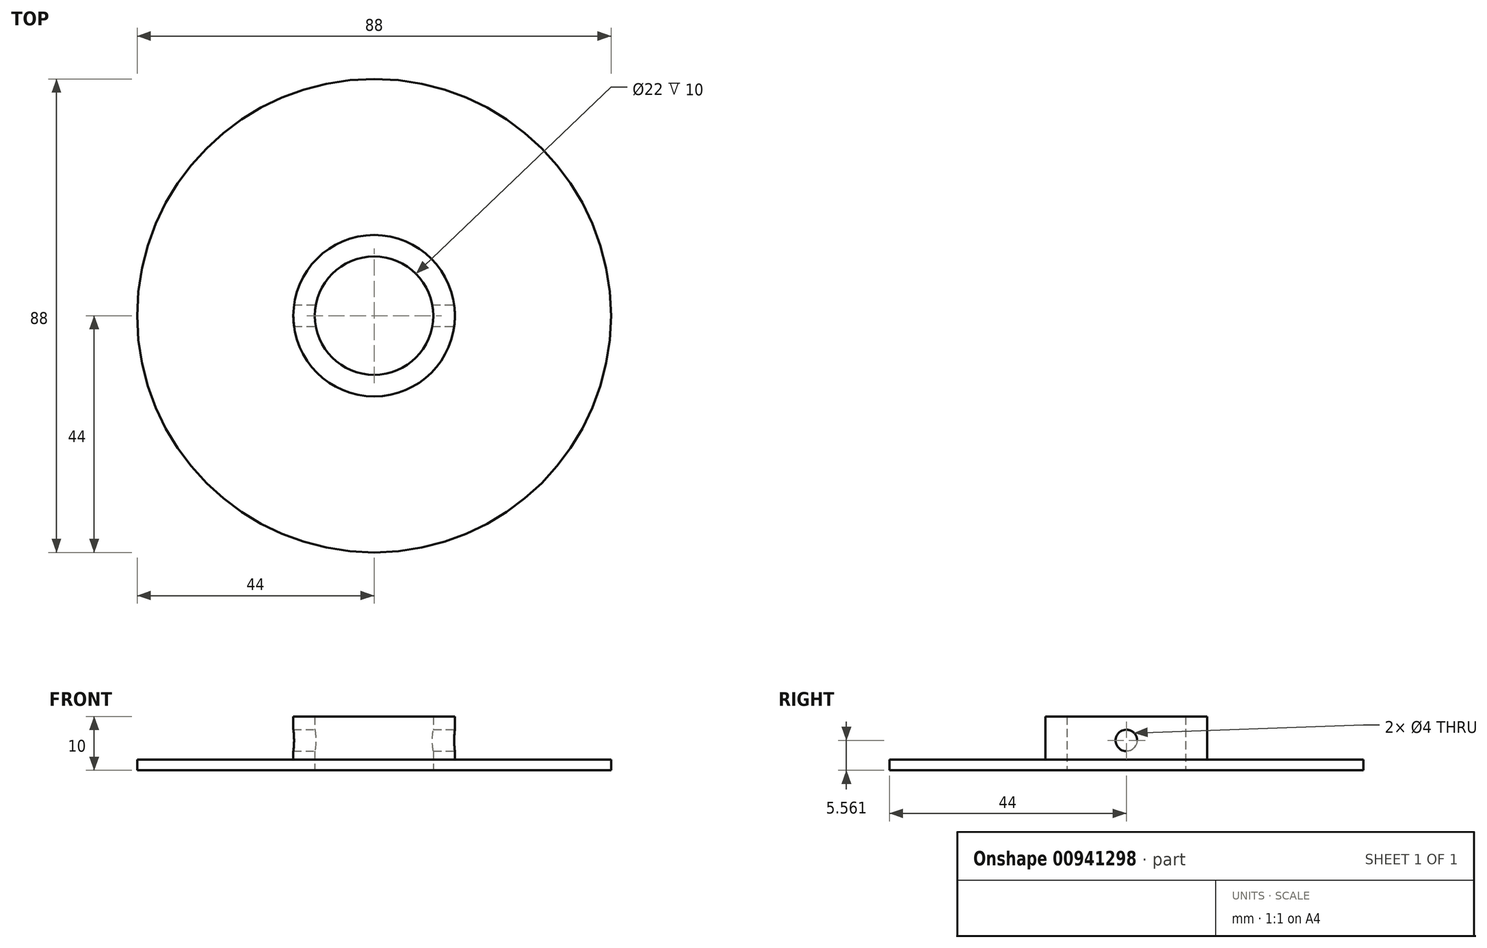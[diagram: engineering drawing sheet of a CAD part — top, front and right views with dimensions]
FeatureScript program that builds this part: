
annotation { "Feature Type Name" : "Feature", "Feature Type Description" : "" }
export const myFeature = defineFeature(function(context is Context, id is Id, definition is map)
    precondition{}
    {
        {
            var Q0;
            Q0=qCreatedBy(makeId("Top.planeOp"),FACE);
            var sketch = newSketch(context, id + "F0", { "sketchPlane" : qUnion([Q0])});
            skCircle(sketch, "E0", {"center": v(0, 0) * mm, "radius": 11 * mm});
            skCircle(sketch, "E1.0", {"center": v(0, 0) * mm, "radius": 15 * mm});
            skCircle(sketch, "E2", {"center": v(0, 0) * mm, "radius": 44 * mm});
            skSolve(sketch);
        }
        {
            var Q0;
            Q0=makeQuery(id+"F0.imprint","IMPRINT",FACE,{"disambiguationData":[TD([[makeQuery(id+"F0.imprint","IMPRINT",EDGE,{"derivedFrom":sQuery(id+"F0.wireOp",EDGE,"E0")}),-1.0]])]});
            extrude(context, id + "F1", {"entities" : qUnion([Q0]), "depth" : 10 * mm, "offsetDistance" : 25 * mm});
        }
        {
            var Q0;
            Q0=makeQuery(id+"F0.imprint","IMPRINT",FACE,{"disambiguationData":[TD([[makeQuery(id+"F0.imprint","IMPRINT",EDGE,{"derivedFrom":sQuery(id+"F0.wireOp",EDGE,"E1.0")}),-1.0]])]});
            extrude(context, id + "F2", {"entities" : qUnion([Q0]), "operationType" : NewBodyOperationType.ADD, "depth" : 2 * mm, "offsetDistance" : 25 * mm});
        }
        {
            var Q0;
            Q0=qCreatedBy(makeId("Right.planeOp"),FACE);
            var sketch = newSketch(context, id + "F3", { "sketchPlane" : qUnion([Q0])});
            skCircle(sketch, "E3", {"center": v(0, 5.56) * mm, "radius": 2 * mm});
            skSolve(sketch);
        }
        {
            var Q0;
            Q0=makeQuery(id+"F3.imprint","IMPRINT",FACE,{"disambiguationData":[TD([[makeQuery(id+"F3.imprint","IMPRINT",EDGE,{"derivedFrom":sQuery(id+"F3.wireOp",EDGE,"E3")}),1.0]])]});
            extrude(context, id + "F4", {"entities" : qUnion([Q0]), "operationType" : NewBodyOperationType.REMOVE, "endBound" : BoundingType.SYMMETRIC, "oppositeDirection" : true, "depth" : 50 * mm, "offsetDistance" : 25 * mm});
        }
    });
